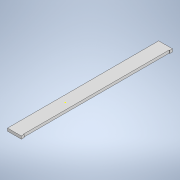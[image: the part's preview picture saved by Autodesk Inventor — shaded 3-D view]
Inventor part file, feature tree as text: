
AUTODESK INVENTOR PART (.ipt)
format: ipt  version: 2020 (Build 240168000, 168)  size: 136,192 bytes
history: native  units: mm
features: sketch x5, extrude x4
ambient origin geometry x8: Origin, YZ Plane, XZ Plane, XY Plane, X Axis, Y Axis, Z Axis, Center Point
bodies: Solid1 (feature_tree)
feature tree (9):
  extrude  "Extrusion1"  Depth=10.0mm
  extrude  "Extrusion2"  Depth=37.0mm
  extrude  "Extrusion3"  Depth=2.0mm
  extrude  "Extrusion4"  Depth=36.0mm TaperAngle=0.0deg
  sketch  "Sketch5"  dims[d11=0.1mm d12=18.25mm d13=0.0mm]
  sketch  "Sketch1"  dims[d0=10.0mm d1=74.0mm]
  sketch  "Sketch2"  dims[d2=5.0mm d3=37.0mm]
  sketch  "Sketch3"  dims[d4=2.0mm d5=0.0mm d6=72.0mm]
  sketch  "Sketch4"  dims[d7=0.3mm d8=0.0mm d9=36.0mm d10=0.0mm]
